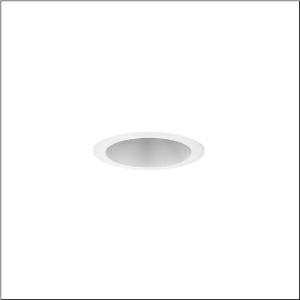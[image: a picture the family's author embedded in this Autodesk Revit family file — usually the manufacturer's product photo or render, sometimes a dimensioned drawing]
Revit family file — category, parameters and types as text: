
# Revit family: lunis_31-l_51dn15ee31b
name_source: partatom
category: Lighting Fixtures
units: mm (PartAtom-declared; Revit-internal decimal feet)

## family parameters
Cut with Voids When Loaded = No
Host = Face
Light Source = No
Part Type = Normal
Room Calculation Point = No
Round Connector Dimension = Use Diameter
Shared = No

## types (1)
- --- (1 x LED, 1650 lm, 12.2 W, 3000K)
    Apparent Load = 12 VA
    CIE Flux Codes = 93 98 100 100 100
    Color Rendering = 80
    Color Temperature = 3000K
    Default Elevation = 1800 mm
    Description = Lunis 31-L, downlight, light control with reflector, light emission: direct distribution, LED rated luminous flux: 1.650lm, light colour: 830, mains connection: 220..240V, AC/DC, 0/50..60Hz, housing, of aluminium, white, protection rating (complete): IP20, protection rating (on room side): IP54, insulation class (complete): insulation class II (safety insulation), certification: CE, ENEC, packaging unit: 1 piece
    Height = 0 mm  [stored 0 ft]
    Lamp = 1 x LED
    Lamp Light Flux = 1650 lm
    Lamp Power = 12.2 W
    Lamp count = 1
    Length = 188 mm  [stored 0.616798 ft]
    Luminous efficacy = 135 lm/W
    Manufacturer = Siteco
    ModVariant = No
    Model = 51DN15EE31B
    Mounting Place = Ceiling
    Mounting Type = Recessed
    Number of Poles = 1
    OnlyDefault = Yes
    Power Factor = 1
    Product Name = Lunis 31-L
    Product group = downlight
    ProductGroupID = 401
    Protection Class = Protection class II
    Protection Degree = IP 20
    RLX_Detail_Level = 1
    RLX_Emergency_Light_Flux = 0 lm
    RLX_Emergency_Type = 0
    RLX_Emergency_Type_DB = No
    RlxData = <blob elided: 22213 chars, md5=9b60be5a>
    Socket = socket
    Standby Power = 0 W
    System Light Flux = 1650 lm
    System Power = 12 W
    Type Comments = individual setting: luminous flux: 100 % | (OFF | ON) | 300 mA
    Type Image = l_1345911.jpg
    URL = http://relux.com
    VarID = @adj_031231
    Voltage = 0 V
    Weight = 0.00 kg
    Width = 0 mm  [stored 0 ft]

note: [stored X ft] marks values corroborated as IEEE doubles in the binary element streams (Revit-internal decimal feet)

## geometry (parser evidence)
native form markers: Blend x4, Sweep x12
no freeform markers — native parametric forms only
